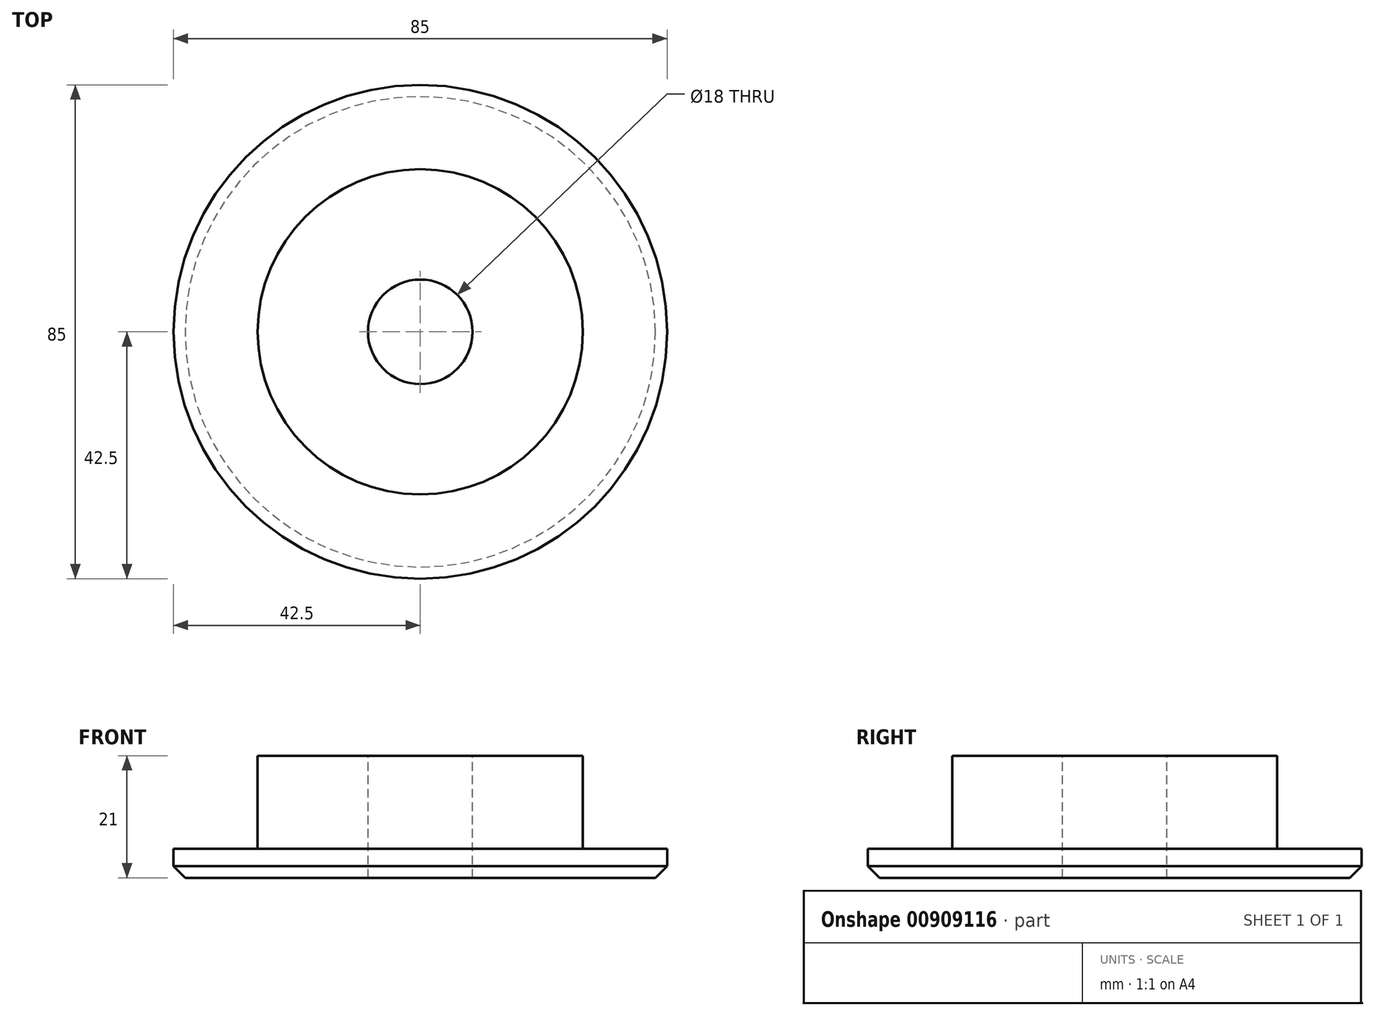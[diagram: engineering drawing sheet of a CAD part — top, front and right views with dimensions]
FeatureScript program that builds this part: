
annotation { "Feature Type Name" : "Feature", "Feature Type Description" : "" }
export const myFeature = defineFeature(function(context is Context, id is Id, definition is map)
    precondition{}
    {
        {
            var Q0;
            Q0=qCreatedBy(makeId("Top.planeOp"),FACE);
            var sketch = newSketch(context, id + "F0", { "sketchPlane" : qUnion([Q0])});
            skCircle(sketch, "E0", {"center": v(0, 0) * mm, "radius": 42.5 * mm});
            skSolve(sketch);
        }
        {
            var Q0;
            Q0 = qSketchRegion(id + "F0", true);
            extrude(context, id + "F1", {"entities" : qUnion([Q0]), "depth" : 5 * mm, "offsetDistance" : 25 * mm});
        }
        {
            var Q0;
            Q0=makeQuery(id+"F1.opExtrude","CAP_FACE",FACE,{"disambiguationData":[OSD([sQuery(id+"F0.wireOp",EDGE,"E0")])],"isStart":false});
            var sketch = newSketch(context, id + "F2", { "sketchPlane" : qUnion([Q0])});
            skCircle(sketch, "E1", {"center": v(0, 0) * mm, "radius": 28 * mm});
            skSolve(sketch);
        }
        {
            var Q0;
            Q0 = qSketchRegion(id + "F2", true);
            extrude(context, id + "F3", {"entities" : qUnion([Q0]), "operationType" : NewBodyOperationType.ADD, "depth" : 16 * mm, "offsetDistance" : 25 * mm});
        }
        {
            var Q0;
            Q0=makeQuery(id+"F3.opExtrude","CAP_FACE",FACE,{"disambiguationData":[OSD([sQuery(id+"F2.wireOp",EDGE,"E1")])],"isStart":false});
            var sketch = newSketch(context, id + "F4", { "sketchPlane" : qUnion([Q0])});
            skCircle(sketch, "E2", {"center": v(0, 0) * mm, "radius": 9 * mm});
            skSolve(sketch);
        }
        {
            var Q0;
            Q0 = qSketchRegion(id + "F4", true);
            extrude(context, id + "F5", {"entities" : qUnion([Q0]), "operationType" : NewBodyOperationType.REMOVE, "endBound" : BoundingType.UP_TO_NEXT, "oppositeDirection" : true, "depth" : 25 * mm, "offsetDistance" : 25 * mm});
        }
        {
            var Q0;
            Q0=makeQuery(id+"F1.opExtrude","CAP_EDGE",EDGE,{"disambiguationData":[OSD([sQuery(id+"F0.wireOp",EDGE,"E0")])],"isStart":true});
            var Q1;
            Q1=makeQuery(id+"F5.boolean.opBoolean","COPY",EDGE,{"derivedFrom":makeQuery(id+"F5.opExtrude","CAP_EDGE",EDGE,{"disambiguationData":[OSD([sQuery(id+"F4.wireOp",EDGE,"E2")])],"isStart":false})});
            var Q2;
            Q2=makeQuery(id+"F5.boolean.opBoolean","COPY",EDGE,{"derivedFrom":makeQuery(id+"F5.opExtrude","CAP_EDGE",EDGE,{"disambiguationData":[OSD([sQuery(id+"F4.wireOp",EDGE,"E2")])],"isStart":true})});
            chamfer(context, id + "F6", {"entities" : qUnion([Q0, Q1, Q2]), "width" : 2 * mm, "tangentPropagation" : true});
        }
    });
